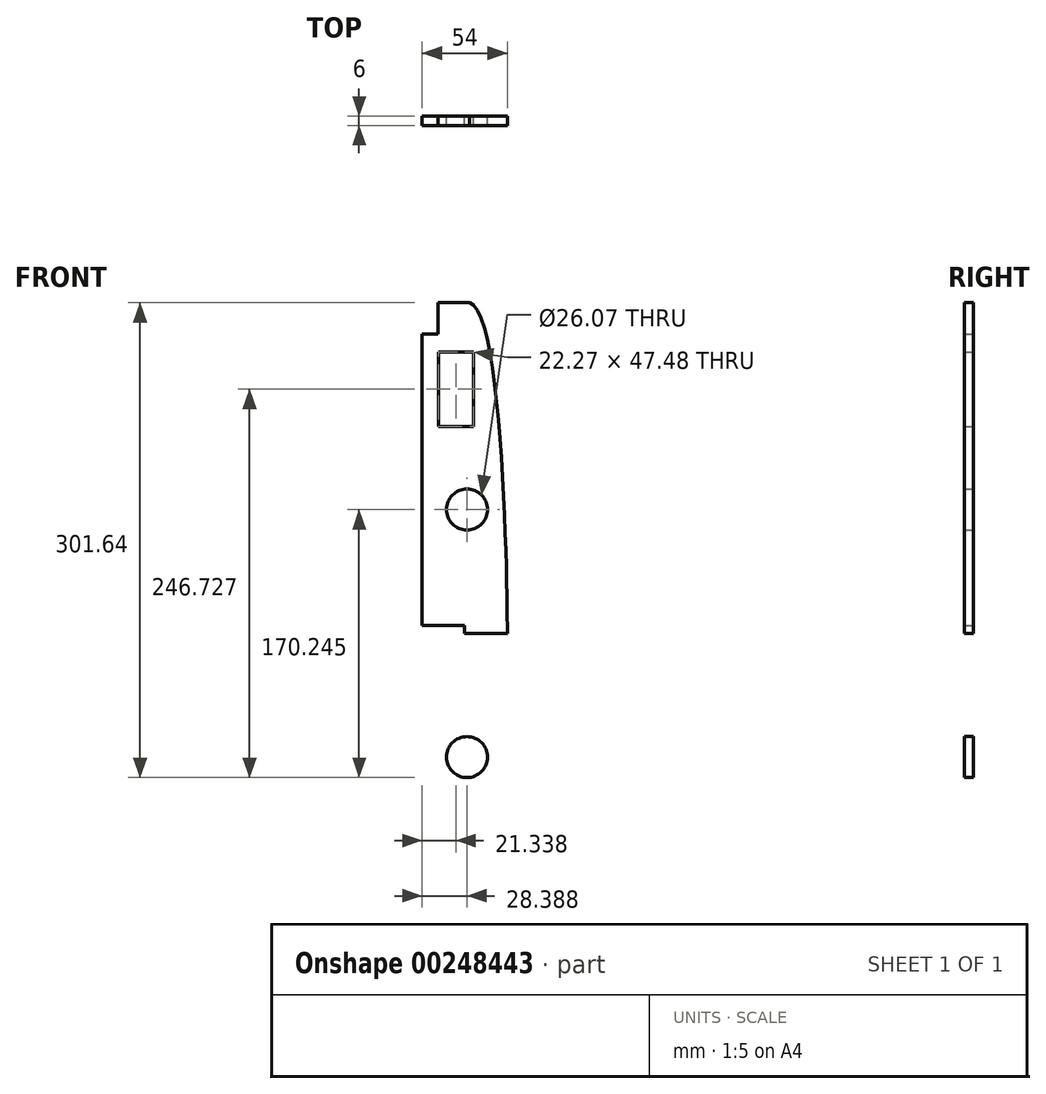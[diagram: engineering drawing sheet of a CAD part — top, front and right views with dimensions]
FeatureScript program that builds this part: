
annotation { "Feature Type Name" : "Feature", "Feature Type Description" : "" }
export const myFeature = defineFeature(function(context is Context, id is Id, definition is map)
    precondition{}
    {
        {
            var Q0;
            Q0=qCreatedBy(makeId("Front.planeOp"),FACE);
            var sketch = newSketch(context, id + "F0", { "sketchPlane" : qUnion([Q0])});
            skLineSegment(sketch, "E0.bottom", {"start": v(135.86, 215) * mm, "end": v(91.86, 215) * mm});
            skLineSegment(sketch, "E0.top", {"start": v(135.86, 5) * mm, "end": v(81.86, 5) * mm});
            skLineSegment(sketch, "E0.left", {"start": v(135.86, 215) * mm, "end": v(135.86, 5) * mm});
            skFitSpline(sketch, "E1", {"points": [v(111.86, 215) * mm, v(135.86, 5) * mm], "startDerivative": vector(72, -18.9) * mm, "endDerivative": vector(-0.42, 27.38) * mm});
            skLineSegment(sketch, "E2.bottom", {"start": v(114.33, 183.83) * mm, "end": v(92.07, 183.83) * mm});
            skLineSegment(sketch, "E2.top", {"start": v(114.33, 136.35) * mm, "end": v(92.07, 136.35) * mm});
            skLineSegment(sketch, "E2.left", {"start": v(114.33, 183.83) * mm, "end": v(114.33, 136.35) * mm});
            skLineSegment(sketch, "E2.right", {"start": v(92.07, 183.83) * mm, "end": v(92.07, 136.35) * mm});
            skCircle(sketch, "E3", {"center": v(110.25, 83.6) * mm, "radius": 13.03 * mm});
            skCircle(sketch, "E4.MirrorC", {"center": v(110.25, -73.6) * mm, "radius": 13.03 * mm});
            skLineSegment(sketch, "E5.MirrorCS", {"start": v(92.07, -173.83) * mm, "end": v(92.07, -126.35) * mm});
            skLineSegment(sketch, "E6.MirrorCS", {"start": v(114.33, -173.83) * mm, "end": v(114.33, -126.35) * mm});
            skLineSegment(sketch, "E7.MirrorCS", {"start": v(114.33, -126.35) * mm, "end": v(92.07, -126.35) * mm});
            skLineSegment(sketch, "E8.MirrorCS", {"start": v(114.33, -173.83) * mm, "end": v(92.07, -173.83) * mm});
            skFitSpline(sketch, "E9.MirrorCS", {"points": [v(111.86, -205) * mm, v(135.86, 5) * mm], "startDerivative": vector(72, 18.9) * mm, "endDerivative": vector(-0.42, -27.38) * mm});
            skLineSegment(sketch, "E10.MirrorCS", {"start": v(135.86, -205) * mm, "end": v(135.86, 5) * mm});
            skLineSegment(sketch, "E11.MirrorCS", {"start": v(135.86, -205) * mm, "end": v(91.86, -205) * mm});
            skLineSegment(sketch, "E12", {"start": v(108.86, 5) * mm, "end": v(108.86, 10) * mm});
            skLineSegment(sketch, "E13", {"start": v(108.86, 5) * mm, "end": v(108.86, 0) * mm});
            skLineSegment(sketch, "E14", {"start": v(108.86, 10) * mm, "end": v(81.86, 10) * mm});
            skLineSegment(sketch, "E15", {"start": v(108.86, 0) * mm, "end": v(81.86, 0) * mm});
            skLineSegment(sketch, "E16", {"start": v(91.86, 215) * mm, "end": v(91.86, 195) * mm});
            skLineSegment(sketch, "E17", {"start": v(91.86, 195) * mm, "end": v(81.86, 195) * mm});
            skLineSegment(sketch, "E18", {"start": v(81.86, 195) * mm, "end": v(81.86, 5) * mm});
            skLineSegment(sketch, "E19.MirrorCS", {"start": v(91.86, -205) * mm, "end": v(91.86, -185) * mm});
            skLineSegment(sketch, "E20.MirrorCS", {"start": v(91.86, -185) * mm, "end": v(81.86, -185) * mm});
            skLineSegment(sketch, "E21", {"start": v(81.86, -185) * mm, "end": v(81.86, 5) * mm});
            skSolve(sketch);
        }
        {
            var Q0;
            Q0=makeQuery(id+"F0.imprint","IMPRINT",FACE,{"disambiguationData":[TD([[makeQuery(id+"F0.imprint","IMPRINT",EDGE,{"derivedFrom":sQuery(id+"F0.wireOp",EDGE,"39521459-0991-4ba8-99ea-7a529d2b0f72")}),1.0]])]});
            var Q1;
            {var subQ8=sQuery(id+"F0.wireOp",EDGE,"58960234-5e6d-4689-94ac-15826fa52e1d");Q1=makeQuery(id+"F0.imprint","IMPRINT",FACE,{"disambiguationData":[TD([[makeQuery(id+"F0.imprint","IMPRINT",EDGE,{"derivedFrom":subQ8}),-1.0]])]});}
            var Q2;
            Q2=makeQuery(id+"F0.imprint","IMPRINT",FACE,{"disambiguationData":[TD([[makeQuery(id+"F0.imprint","IMPRINT",EDGE,{"derivedFrom":sQuery(id+"F0.wireOp",EDGE,"E4.MirrorC")}),1.0]])]});
            var Q3;
            Q3=makeQuery(id+"F0.imprint","IMPRINT",FACE,{"disambiguationData":[TD([[makeQuery(id+"F0.imprint","IMPRINT",EDGE,{"derivedFrom":sQuery(id+"F0.wireOp",EDGE,"E2.bottom")}),-1.0]])]});
            extrude(context, id + "F1", {"entities" : qUnion([Q0, Q1, Q2, Q3]), "depth" : 6 * mm});
        }
    });
